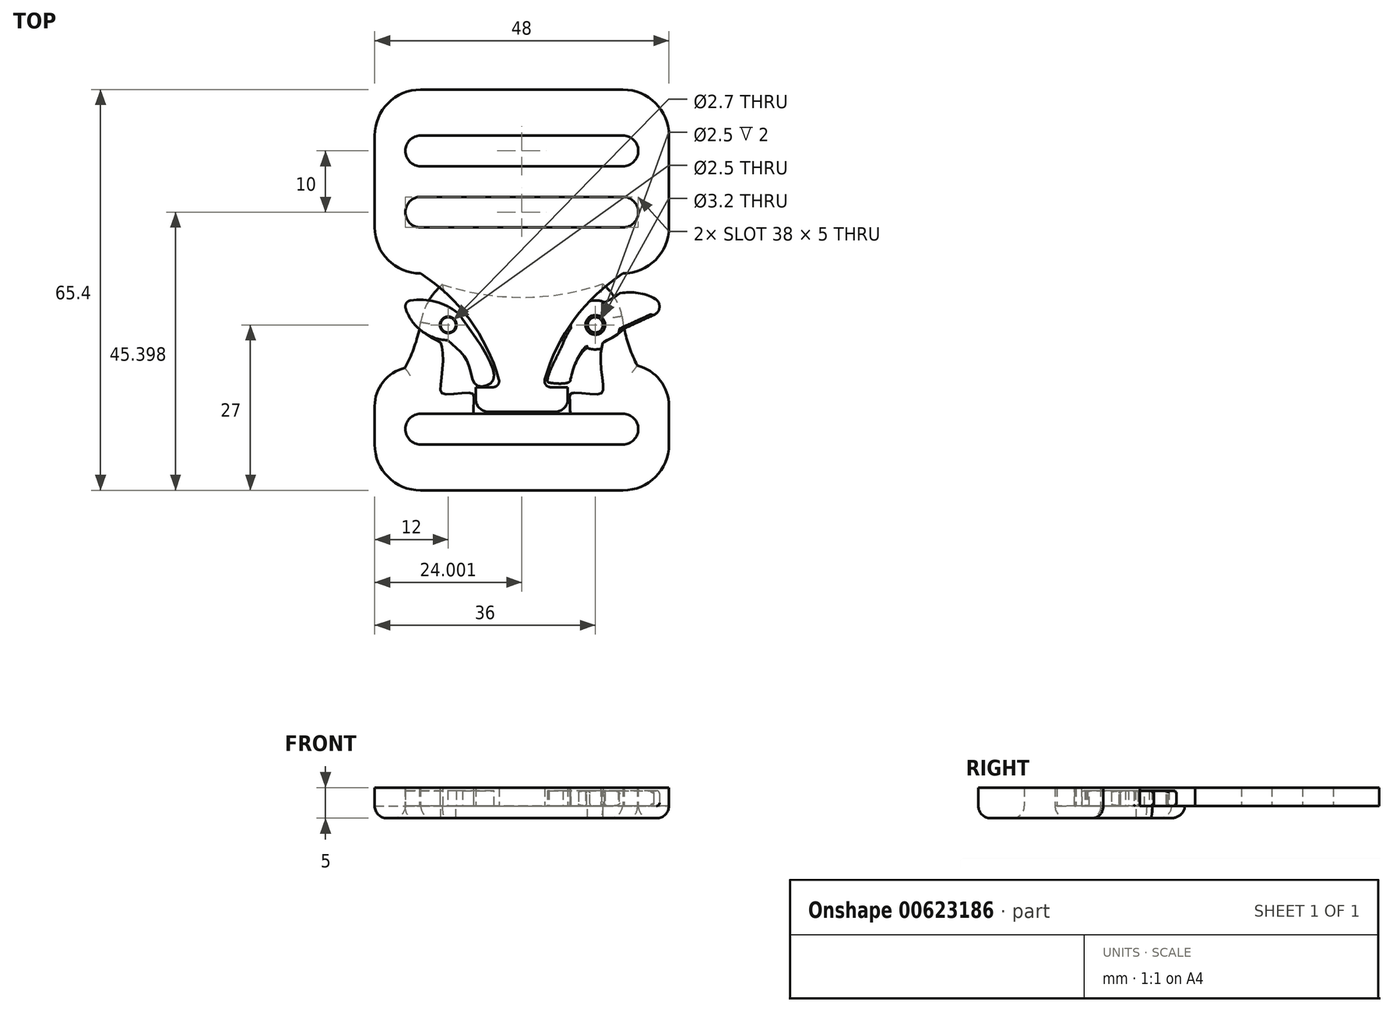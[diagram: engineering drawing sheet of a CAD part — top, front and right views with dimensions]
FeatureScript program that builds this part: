
annotation { "Feature Type Name" : "Feature", "Feature Type Description" : "" }
export const myFeature = defineFeature(function(context is Context, id is Id, definition is map)
    precondition{}
    {
        {
            var Q0;
            Q0=qCreatedBy(makeId("Top.planeOp"),FACE);
            var sketch = newSketch(context, id + "F0", { "sketchPlane" : qUnion([Q0])});
            skLineSegment(sketch, "E0.bottom", {"start": v(16.5, 2.5) * mm, "end": v(-16.5, 2.5) * mm});
            skLineSegment(sketch, "E0.top", {"start": v(16.5, -2.5) * mm, "end": v(-16.5, -2.5) * mm});
            skLineSegment(sketch, "E0.left", {"start": v(19, 0) * mm, "end": v(19, 0) * mm});
            skLineSegment(sketch, "E0.right", {"start": v(-19, 0) * mm, "end": v(-19, 0) * mm});
            skPoint(sketch, "E0.middle", {"position": v(0, 0) * mm});
            skPoint(sketch, "E1.visualSharp", {"position": v(-19, 2.5) * mm});
            skArc(sketch, "E1.filletArc", {"start": v(-16.5, 2.5) * mm, "mid": v(-18.27, 1.77) * mm, "end": v(-19, 0) * mm});
            skPoint(sketch, "E2.visualSharp", {"position": v(-19, -2.5) * mm});
            skArc(sketch, "E2.filletArc", {"start": v(-19, 0) * mm, "mid": v(-18.27, -1.77) * mm, "end": v(-16.5, -2.5) * mm});
            skPoint(sketch, "E3.visualSharp", {"position": v(19, -2.5) * mm});
            skArc(sketch, "E3.filletArc", {"start": v(16.5, -2.5) * mm, "mid": v(18.27, -1.77) * mm, "end": v(19, 0) * mm});
            skPoint(sketch, "E4.visualSharp", {"position": v(19, 2.5) * mm});
            skArc(sketch, "E4.filletArc", {"start": v(19, 0) * mm, "mid": v(18.27, 1.77) * mm, "end": v(16.5, 2.5) * mm});
            skLineSegment(sketch, "E5.bottom", {"start": v(16.5, -10) * mm, "end": v(-16.5, -10) * mm});
            skLineSegment(sketch, "E5.left", {"start": v(24, -2.5) * mm, "end": v(24, 3.75) * mm});
            skLineSegment(sketch, "E5.right", {"start": v(-24, -2.5) * mm, "end": v(-24, 3.75) * mm});
            skPoint(sketch, "E6.visualSharp", {"position": v(-24, -10) * mm});
            skArc(sketch, "E6.filletArc", {"start": v(-24, -2.5) * mm, "mid": v(-21.8, -7.8) * mm, "end": v(-16.5, -10) * mm});
            skPoint(sketch, "E7.visualSharp", {"position": v(24, -10) * mm});
            skArc(sketch, "E7.filletArc", {"start": v(16.5, -10) * mm, "mid": v(21.8, -7.8) * mm, "end": v(24, -2.5) * mm});
            skArc(sketch, "E8", {"start": v(-12.96, 23.6) * mm, "mid": v(0.12, 21.5) * mm, "end": v(13.2, 23.68) * mm});
            skLineSegment(sketch, "E9", {"start": v(0, 21.5) * mm, "end": v(0, 0) * mm, "construction": true});
            skArc(sketch, "E10", {"start": v(16.36, 18.4) * mm, "mid": v(17.24, 14.28) * mm, "end": v(18.84, 10.38) * mm});
            skArc(sketch, "E11", {"start": v(-19.07, 9.97) * mm, "mid": v(-17.47, 13.6) * mm, "end": v(-16.5, 17.47) * mm});
            skArc(sketch, "E12", {"start": v(16.5, 17.47) * mm, "mid": v(15.46, 20.9) * mm, "end": v(13.2, 23.68) * mm});
            skArc(sketch, "E13", {"start": v(-12.96, 23.6) * mm, "mid": v(-15.25, 20.83) * mm, "end": v(-16.5, 17.47) * mm});
            skArc(sketch, "E14", {"start": v(24, 3.75) * mm, "mid": v(22.56, 7.95) * mm, "end": v(18.84, 10.38) * mm});
            skArc(sketch, "E15", {"start": v(-19.07, 9.97) * mm, "mid": v(-22.62, 7.72) * mm, "end": v(-24, 3.75) * mm});
            skSolve(sketch);
        }
        {
            var Q0;
            Q0=qSketchRegion(id+"F0",true);
            extrude(context, id + "F1", {"entities" : qUnion([Q0]), "depth" : 2 * mm, "offsetDistance" : 25 * mm});
        }
        {
            var Q0;
            Q0=makeQuery(id+"F1.opExtrude","CAP_FACE",FACE,{"disambiguationData":[OSD([sQuery(id+"F0.wireOp",EDGE,"E0.bottom"),sQuery(id+"F0.wireOp",EDGE,"E0.top"),sQuery(id+"F0.wireOp",EDGE,"E1.filletArc"),sQuery(id+"F0.wireOp",EDGE,"E2.filletArc"),sQuery(id+"F0.wireOp",EDGE,"E3.filletArc"),sQuery(id+"F0.wireOp",EDGE,"E4.filletArc"),sQuery(id+"F0.wireOp",EDGE,"E5.bottom"),sQuery(id+"F0.wireOp",EDGE,"E5.left"),sQuery(id+"F0.wireOp",EDGE,"E5.right"),sQuery(id+"F0.wireOp",EDGE,"E6.filletArc"),sQuery(id+"F0.wireOp",EDGE,"E7.filletArc"),sQuery(id+"F0.wireOp",EDGE,"iaLIUP0t-tZGx-AWgD-4cdN-IuAON2PRfYnM.left"),sQuery(id+"F0.wireOp",EDGE,"iaLIUP0t-tZGx-AWgD-4cdN-IuAON2PRfYnM.right"),sQuery(id+"F0.wireOp",EDGE,"ac3eb495-d787-4141-9d20-389c025eaae5.filletArc"),sQuery(id+"F0.wireOp",EDGE,"95ab88b0-9d58-4345-83fa-b843aa859d97.filletArc"),sQuery(id+"F0.wireOp",EDGE,"E8")])],"isStart":false});
            var sketch = newSketch(context, id + "F2", { "sketchPlane" : qUnion([Q0])});
            skLineSegment(sketch, "E16.bottom", {"start": v(-16.5, 42.9) * mm, "end": v(16.5, 42.9) * mm});
            skLineSegment(sketch, "E16.top", {"start": v(-16.5, 47.9) * mm, "end": v(16.5, 47.9) * mm});
            skLineSegment(sketch, "E16.left", {"start": v(19, -8.96) * mm, "end": v(19, -8.96) * mm});
            skLineSegment(sketch, "E16.right", {"start": v(-19, -8.96) * mm, "end": v(-19, -8.96) * mm});
            skPoint(sketch, "E16.middle", {"position": v(0, 45.4) * mm});
            skPoint(sketch, "E17.visualSharp", {"position": v(19, 42.9) * mm});
            skArc(sketch, "E17.filletArc", {"start": v(16.5, 42.9) * mm, "mid": v(18.27, 43.63) * mm, "end": v(19, 45.4) * mm});
            skPoint(sketch, "E18.visualSharp", {"position": v(19, 47.9) * mm});
            skArc(sketch, "E18.filletArc", {"start": v(19, 45.4) * mm, "mid": v(18.27, 47.17) * mm, "end": v(16.5, 47.9) * mm});
            skPoint(sketch, "E19.visualSharp", {"position": v(-19, 47.9) * mm});
            skArc(sketch, "E19.filletArc", {"start": v(-16.5, 47.9) * mm, "mid": v(-18.27, 47.17) * mm, "end": v(-19, 45.4) * mm});
            skPoint(sketch, "E20.visualSharp", {"position": v(-19, 42.9) * mm});
            skArc(sketch, "E20.filletArc", {"start": v(-19, 45.4) * mm, "mid": v(-18.27, 43.63) * mm, "end": v(-16.5, 42.9) * mm});
            skLineSegment(sketch, "E21.bottom", {"start": v(-16.5, 55.4) * mm, "end": v(16.5, 55.4) * mm});
            skLineSegment(sketch, "E21.left", {"start": v(-24, 47.9) * mm, "end": v(-24, 35.4) * mm});
            skLineSegment(sketch, "E21.right", {"start": v(24, 47.9) * mm, "end": v(24, 35.4) * mm});
            skPoint(sketch, "E22.visualSharp", {"position": v(24, 55.4) * mm});
            skArc(sketch, "E22.filletArc", {"start": v(24, 47.9) * mm, "mid": v(21.8, 53.2) * mm, "end": v(16.5, 55.4) * mm});
            skPoint(sketch, "E23.visualSharp", {"position": v(-24, 55.4) * mm});
            skArc(sketch, "E23.filletArc", {"start": v(-16.5, 55.4) * mm, "mid": v(-21.8, 53.2) * mm, "end": v(-24, 47.9) * mm});
            skLineSegment(sketch, "E24.left", {"start": v(24, 35.4) * mm, "end": v(24, 32.9) * mm});
            skLineSegment(sketch, "E24.right", {"start": v(-24, 35.4) * mm, "end": v(-24, 32.9) * mm});
            skPoint(sketch, "E25.visualSharp", {"position": v(24, 20.4) * mm});
            skArc(sketch, "E25.filletArc", {"start": v(16.5, 25.4) * mm, "mid": v(21.8, 27.6) * mm, "end": v(24, 32.9) * mm});
            skPoint(sketch, "E26.visualSharp", {"position": v(-24, 20.4) * mm});
            skArc(sketch, "E26.filletArc", {"start": v(-24, 32.9) * mm, "mid": v(-21.8, 27.6) * mm, "end": v(-16.5, 25.4) * mm});
            skLineSegment(sketch, "E27", {"start": v(0, 45.4) * mm, "end": v(0, 35.4) * mm, "construction": true});
            skPoint(sketch, "E27.endSnap0", {"position": v(0, 42.9) * mm});
            skLineSegment(sketch, "E28.bottom", {"start": v(-16.5, 37.9) * mm, "end": v(16.5, 37.9) * mm});
            skLineSegment(sketch, "E28.top", {"start": v(-16.5, 32.9) * mm, "end": v(16.5, 32.9) * mm});
            skLineSegment(sketch, "E28.left", {"start": v(19, 1.04) * mm, "end": v(19, 1.04) * mm});
            skLineSegment(sketch, "E28.right", {"start": v(-19, 1.04) * mm, "end": v(-19, 1.04) * mm});
            skPoint(sketch, "E28.middle", {"position": v(0, 35.4) * mm});
            skPoint(sketch, "E29.visualSharp", {"position": v(19, 32.9) * mm});
            skArc(sketch, "E29.filletArc", {"start": v(16.5, 32.9) * mm, "mid": v(18.27, 33.63) * mm, "end": v(19, 35.4) * mm});
            skPoint(sketch, "E30.visualSharp", {"position": v(19, 37.9) * mm});
            skArc(sketch, "E30.filletArc", {"start": v(19, 35.4) * mm, "mid": v(18.27, 37.17) * mm, "end": v(16.5, 37.9) * mm});
            skPoint(sketch, "E31.visualSharp", {"position": v(-19, 37.9) * mm});
            skArc(sketch, "E31.filletArc", {"start": v(-16.5, 37.9) * mm, "mid": v(-18.27, 37.17) * mm, "end": v(-19, 35.4) * mm});
            skPoint(sketch, "E32.visualSharp", {"position": v(-19, 32.9) * mm});
            skArc(sketch, "E32.filletArc", {"start": v(-19, 35.4) * mm, "mid": v(-18.27, 33.63) * mm, "end": v(-16.5, 32.9) * mm});
            skArc(sketch, "E33", {"start": v(-16.5, 25.4) * mm, "mid": v(0, 21.84) * mm, "end": v(16.5, 25.4) * mm, "construction": true});
            skLineSegment(sketch, "E34", {"start": v(16.5, 25.4) * mm, "end": v(-16.5, 25.4) * mm, "construction": true});
            skLineSegment(sketch, "E35", {"start": v(0, 21.84) * mm, "end": v(0, 4.84) * mm, "construction": true});
            skPoint(sketch, "E35.endSnap0", {"position": v(0, 21.84) * mm});
            skLineSegment(sketch, "E36.bottom", {"start": v(7.5, 6.84) * mm, "end": v(4.7, 6.84) * mm});
            skLineSegment(sketch, "E36.top", {"start": v(5.5, 2.84) * mm, "end": v(-5.5, 2.84) * mm});
            skLineSegment(sketch, "E36.left", {"start": v(7.5, 6.84) * mm, "end": v(7.5, 4.84) * mm});
            skLineSegment(sketch, "E36.right", {"start": v(-7.5, 6.84) * mm, "end": v(-7.5, 4.84) * mm});
            skPoint(sketch, "E36.middle", {"position": v(0, 4.84) * mm});
            skLineSegment(sketch, "E37", {"start": v(16.5, 25.4) * mm, "end": v(16.5, 55.4) * mm, "construction": true});
            skLineSegment(sketch, "E38", {"start": v(-16.5, 25.4) * mm, "end": v(-16.5, 55.4) * mm, "construction": true});
            skPoint(sketch, "E39.visualSharp", {"position": v(7.5, 2.84) * mm});
            skArc(sketch, "E39.filletArc", {"start": v(5.5, 2.84) * mm, "mid": v(6.91, 3.42) * mm, "end": v(7.5, 4.84) * mm});
            skPoint(sketch, "E40.visualSharp", {"position": v(-7.5, 2.84) * mm});
            skArc(sketch, "E40.filletArc", {"start": v(-7.5, 4.84) * mm, "mid": v(-6.91, 3.42) * mm, "end": v(-5.5, 2.84) * mm});
            skLineSegment(sketch, "E41", {"start": v(0, 4.84) * mm, "end": v(3, 4.84) * mm, "construction": true});
            skLineSegment(sketch, "E42", {"start": v(0, 4.84) * mm, "end": v(-3, 4.84) * mm, "construction": true});
            skArc(sketch, "E43", {"start": v(16.5, 25.4) * mm, "mid": v(8.57, 17.9) * mm, "end": v(3.75, 8.11) * mm});
            skArc(sketch, "E44", {"start": v(-3.73, 8.1) * mm, "mid": v(-8.54, 17.91) * mm, "end": v(-16.5, 25.4) * mm});
            skLineSegment(sketch, "E45.trimOffspring", {"start": v(-4.7, 6.84) * mm, "end": v(-7.5, 6.84) * mm});
            skPoint(sketch, "E46.visualSharp", {"position": v(3.41, 6.84) * mm});
            skArc(sketch, "E46.filletArc", {"start": v(3.75, 8.11) * mm, "mid": v(3.91, 7.23) * mm, "end": v(4.7, 6.84) * mm});
            skPoint(sketch, "E47.visualSharp", {"position": v(-3.4, 6.84) * mm});
            skArc(sketch, "E47.filletArc", {"start": v(-4.7, 6.84) * mm, "mid": v(-3.9, 7.23) * mm, "end": v(-3.73, 8.1) * mm});
            skSolve(sketch);
        }
        {
            var Q0;
            Q0=qSketchRegion(id+"F2",true);
            extrude(context, id + "F3", {"entities" : qUnion([Q0]), "depth" : 3 * mm, "offsetDistance" : 25 * mm});
        }
        {
            var Q0;
            Q0=makeQuery(id+"F1.opExtrude","CAP_FACE",FACE,{"disambiguationData":[OSD([sQuery(id+"F0.wireOp",EDGE,"E0.bottom"),sQuery(id+"F0.wireOp",EDGE,"E0.top"),sQuery(id+"F0.wireOp",EDGE,"E1.filletArc"),sQuery(id+"F0.wireOp",EDGE,"E2.filletArc"),sQuery(id+"F0.wireOp",EDGE,"E3.filletArc"),sQuery(id+"F0.wireOp",EDGE,"E4.filletArc"),sQuery(id+"F0.wireOp",EDGE,"E5.bottom"),sQuery(id+"F0.wireOp",EDGE,"E5.left"),sQuery(id+"F0.wireOp",EDGE,"E5.right"),sQuery(id+"F0.wireOp",EDGE,"E6.filletArc"),sQuery(id+"F0.wireOp",EDGE,"E7.filletArc"),sQuery(id+"F0.wireOp",EDGE,"E8"),sQuery(id+"F0.wireOp",EDGE,"E10"),sQuery(id+"F0.wireOp",EDGE,"E11"),sQuery(id+"F0.wireOp",EDGE,"E12"),sQuery(id+"F0.wireOp",EDGE,"E13"),sQuery(id+"F0.wireOp",EDGE,"E14"),sQuery(id+"F0.wireOp",EDGE,"E15")])],"isStart":false});
            var sketch = newSketch(context, id + "F4", { "sketchPlane" : qUnion([Q0])});
            skArc(sketch, "E48.0.2", {"start": v(-16.71, 16.34) * mm, "mid": v(-17.66, 13.07) * mm, "end": v(-19.07, 9.97) * mm});
            skArc(sketch, "E48.0.3", {"start": v(-19.07, 9.97) * mm, "mid": v(-22.62, 7.72) * mm, "end": v(-24, 3.75) * mm});
            skLineSegment(sketch, "E48.0.4", {"start": v(-24, 3.75) * mm, "end": v(-24, -2.5) * mm});
            skArc(sketch, "E48.0.5", {"start": v(-24, -2.5) * mm, "mid": v(-21.8, -7.8) * mm, "end": v(-16.5, -10) * mm});
            skLineSegment(sketch, "E48.0.6", {"start": v(-16.5, -10) * mm, "end": v(16.5, -10) * mm});
            skArc(sketch, "E48.0.7", {"start": v(16.5, -10) * mm, "mid": v(21.8, -7.8) * mm, "end": v(24, -2.5) * mm});
            skLineSegment(sketch, "E48.0.8", {"start": v(24, -2.5) * mm, "end": v(24, 3.75) * mm});
            skArc(sketch, "E48.0.9", {"start": v(24, 3.75) * mm, "mid": v(22.56, 7.95) * mm, "end": v(18.84, 10.38) * mm});
            skArc(sketch, "E48.0.10", {"start": v(18.84, 10.38) * mm, "mid": v(17.57, 13.28) * mm, "end": v(16.7, 16.33) * mm});
            skFitSpline(sketch, "E49", {"points": [v(16.79, 16.4) * mm, v(15.52, 15.41) * mm, v(13.35, 14.18) * mm, v(13.27, 14.13) * mm, v(12.86, 11.88) * mm, v(13.27, 6.62) * mm, v(12.68, 5.7) * mm, v(8.19, 5.85) * mm, v(7.83, 5.04) * mm, v(7.92, 2) * mm], "startDerivative": vector(-10.18, -9.13) * mm, "endDerivative": vector(0.88, -25.22) * mm});
            skLineSegment(sketch, "E50", {"start": v(0, 0) * mm, "end": v(0, 16.05) * mm, "construction": true});
            skFitSpline(sketch, "E51.MirrorCS", {"points": [v(-16.79, 16.4) * mm, v(-15.52, 15.41) * mm, v(-13.35, 14.18) * mm, v(-13.27, 14.13) * mm, v(-12.86, 11.88) * mm, v(-13.27, 6.62) * mm, v(-12.68, 5.7) * mm, v(-8.19, 5.85) * mm, v(-7.83, 5.04) * mm, v(-7.92, 2) * mm], "startDerivative": vector(10.18, -9.13) * mm, "endDerivative": vector(-0.88, -25.22) * mm});
            skPoint(sketch, "E48.0.11.end.orphan", {"position": v(13.2, 23.68) * mm});
            skPoint(sketch, "E52.orphan", {"position": v(16.36, 18.4) * mm});
            skPoint(sketch, "E48.0.1.start.orphan", {"position": v(-12.96, 23.6) * mm});
            skPoint(sketch, "E53.orphan", {"position": v(-16.5, 17.47) * mm});
            skSolve(sketch);
        }
        {
            var Q0;
            {var subQ4=sQuery(id+"F4.wireOp",EDGE,"E48.0.2");Q0=makeQuery(id+"F4.imprint","IMPRINT",FACE,{"disambiguationData":[TD([[makeQuery(id+"F4.imprint","IMPRINT",EDGE,{"derivedFrom":subQ4}),-1.0]])]});}
            extrude(context, id + "F5", {"entities" : qUnion([Q0]), "operationType" : NewBodyOperationType.ADD, "depth" : 3 * mm, "offsetDistance" : 25 * mm});
        }
        {
            var Q0;
            Q0=makeQuery(id+"F2.imprint","IMPRINT",FACE,{"disambiguationData":[TD([[makeQuery(id+"F2.imprint","IMPRINT",EDGE,{"derivedFrom":sQuery(id+"F2.wireOp",EDGE,"E36.bottom")}),-1.0]])]});
            var sketch = newSketch(context, id + "F6", { "sketchPlane" : qUnion([Q0])});
            skLineSegment(sketch, "E54", {"start": v(0, 0) * mm, "end": v(0, 17) * mm, "construction": true});
            skLineSegment(sketch, "E55", {"start": v(0, 17) * mm, "end": v(12, 17) * mm, "construction": true});
            skLineSegment(sketch, "E56", {"start": v(0, 17) * mm, "end": v(-12, 17) * mm, "construction": true});
            skLineSegment(sketch, "E57", {"start": v(11.27, 19.4) * mm, "end": v(11.27, 19.4) * mm});
            skArc(sketch, "E58", {"start": v(-12.1, 14.5) * mm, "mid": v(-9.66, 16.13) * mm, "end": v(-10.44, 18.96) * mm});
            skLineSegment(sketch, "E59", {"start": v(0, 20) * mm, "end": v(21, 20) * mm, "construction": true});
            skLineSegment(sketch, "E60", {"start": v(0, 20) * mm, "end": v(-18, 20) * mm, "construction": true});
            skArc(sketch, "E61", {"start": v(-18.16, 20.99) * mm, "mid": v(-18.85, 20.52) * mm, "end": v(-18.95, 19.7) * mm});
            skLineSegment(sketch, "E62", {"start": v(0, 17) * mm, "end": v(0, 20) * mm, "construction": true});
            skArc(sketch, "E63", {"start": v(21.5, 18.6) * mm, "mid": v(21.61, 18.67) * mm, "end": v(21.73, 18.73) * mm});
            skArc(sketch, "E64", {"start": v(-18.95, 19.7) * mm, "mid": v(-16.34, 16.02) * mm, "end": v(-12.1, 14.5) * mm});
            skArc(sketch, "E65", {"start": v(-10.44, 18.96) * mm, "mid": v(-14.09, 20.78) * mm, "end": v(-18.16, 20.99) * mm});
            skCircle(sketch, "E66", {"center": v(12, 17) * mm, "radius": 1.6 * mm});
            skCircle(sketch, "E67", {"center": v(-12, 17) * mm, "radius": 1.35 * mm});
            skFitSpline(sketch, "E68", {"points": [v(-10.44, 18.96) * mm, v(-4.72, 7.9) * mm, v(-7.43, 7.2) * mm, v(-8.69, 10.61) * mm, v(-12.1, 14.5) * mm], "startDerivative": vector(26.9, -36.54) * mm, "endDerivative": vector(-17.44, 14.5) * mm});
            skFitSpline(sketch, "E69", {"points": [v(6.74, 14) * mm, v(4.4, 7.58) * mm, v(7.49, 10.39) * mm], "startDerivative": vector(-1.72, -5.28) * mm, "endDerivative": vector(-7, -0.02) * mm});
            skFitSpline(sketch, "E70", {"points": [v(12.96, 14.7) * mm, v(21.5, 18.6) * mm], "startDerivative": vector(0.83, 0.4) * mm, "endDerivative": vector(0.83, 0.4) * mm});
            skFitSpline(sketch, "E71", {"points": [v(4.4, 7.58) * mm, v(6.08, 7.42) * mm, v(7.9, 7.86) * mm, v(7.43, 10.4) * mm], "startDerivative": vector(5.45, -0.72) * mm, "endDerivative": vector(0.06, 9.56) * mm});
            skArc(sketch, "E72", {"start": v(21.78, 21.25) * mm, "mid": v(18.94, 22.22) * mm, "end": v(15.94, 22.14) * mm});
            skArc(sketch, "E73", {"start": v(21.6, 18.66) * mm, "mid": v(22.46, 19.9) * mm, "end": v(21.78, 21.25) * mm});
            skPoint(sketch, "E74", {"position": v(15.94, 22.14) * mm});
            skArc(sketch, "E75", {"start": v(11.84, 20) * mm, "mid": v(13.98, 20.9) * mm, "end": v(15.94, 22.14) * mm});
            skPoint(sketch, "E76", {"position": v(4.6, 9.42) * mm});
            skArc(sketch, "E77", {"start": v(4.6, 9.42) * mm, "mid": v(4.57, 9) * mm, "end": v(4.65, 8.58) * mm});
            skPoint(sketch, "E78", {"position": v(4.65, 8.58) * mm});
            skPoint(sketch, "E79", {"position": v(6.98, 7.46) * mm});
            skArc(sketch, "E80", {"start": v(4.65, 8.58) * mm, "mid": v(5.7, 7.8) * mm, "end": v(6.98, 7.46) * mm});
            skArc(sketch, "E81", {"start": v(11.84, 20) * mm, "mid": v(8.76, 17.45) * mm, "end": v(6.74, 14) * mm});
            skArc(sketch, "E82", {"start": v(9.25, 11.72) * mm, "mid": v(8.42, 9.84) * mm, "end": v(7.9, 7.86) * mm});
            skArc(sketch, "E83", {"start": v(12.96, 14.7) * mm, "mid": v(10.87, 13.5) * mm, "end": v(9.25, 11.72) * mm});
            skSolve(sketch);
        }
        {
            var Q0;
            Q0=qSketchRegion(id+"F6",true);
            extrude(context, id + "F7", {"entities" : qUnion([Q0]), "depth" : 2.5 * mm, "offsetDistance" : 25 * mm});
        }
        {
            var Q0;
            Q0=makeQuery(id+"F1.opExtrude","CAP_FACE",FACE,{"disambiguationData":[OSD([sQuery(id+"F0.wireOp",EDGE,"E0.bottom"),sQuery(id+"F0.wireOp",EDGE,"E0.top"),sQuery(id+"F0.wireOp",EDGE,"E1.filletArc"),sQuery(id+"F0.wireOp",EDGE,"E2.filletArc"),sQuery(id+"F0.wireOp",EDGE,"E3.filletArc"),sQuery(id+"F0.wireOp",EDGE,"E4.filletArc"),sQuery(id+"F0.wireOp",EDGE,"E5.bottom"),sQuery(id+"F0.wireOp",EDGE,"E5.left"),sQuery(id+"F0.wireOp",EDGE,"E5.right"),sQuery(id+"F0.wireOp",EDGE,"E6.filletArc"),sQuery(id+"F0.wireOp",EDGE,"E7.filletArc"),sQuery(id+"F0.wireOp",EDGE,"E8"),sQuery(id+"F0.wireOp",EDGE,"E10"),sQuery(id+"F0.wireOp",EDGE,"E11"),sQuery(id+"F0.wireOp",EDGE,"E12"),sQuery(id+"F0.wireOp",EDGE,"E13"),sQuery(id+"F0.wireOp",EDGE,"E14"),sQuery(id+"F0.wireOp",EDGE,"E15")])],"isStart":true});
            fillet(context, id + "F8", {"entities" : qUnion([Q0]), "radius" : 2 * mm, "tangentPropagation" : true, "allowEdgeOverflow" : false});
        }
        {
            var Q0;
            Q0=makeQuery(id+"F1.opExtrude","CAP_FACE",FACE,{"disambiguationData":[OSD([sQuery(id+"F0.wireOp",EDGE,"E0.bottom"),sQuery(id+"F0.wireOp",EDGE,"E0.top"),sQuery(id+"F0.wireOp",EDGE,"E1.filletArc"),sQuery(id+"F0.wireOp",EDGE,"E2.filletArc"),sQuery(id+"F0.wireOp",EDGE,"E3.filletArc"),sQuery(id+"F0.wireOp",EDGE,"E4.filletArc"),sQuery(id+"F0.wireOp",EDGE,"E5.bottom"),sQuery(id+"F0.wireOp",EDGE,"E5.left"),sQuery(id+"F0.wireOp",EDGE,"E5.right"),sQuery(id+"F0.wireOp",EDGE,"E6.filletArc"),sQuery(id+"F0.wireOp",EDGE,"E7.filletArc"),sQuery(id+"F0.wireOp",EDGE,"E8"),sQuery(id+"F0.wireOp",EDGE,"E10"),sQuery(id+"F0.wireOp",EDGE,"E11"),sQuery(id+"F0.wireOp",EDGE,"E12"),sQuery(id+"F0.wireOp",EDGE,"E13"),sQuery(id+"F0.wireOp",EDGE,"E14"),sQuery(id+"F0.wireOp",EDGE,"E15")])],"isStart":false});
            var sketch = newSketch(context, id + "F9", { "sketchPlane" : qUnion([Q0])});
            skLineSegment(sketch, "E84", {"start": v(0, 0) * mm, "end": v(0, 17) * mm, "construction": true});
            skLineSegment(sketch, "E85", {"start": v(0, 17) * mm, "end": v(12, 17) * mm, "construction": true});
            skLineSegment(sketch, "E86", {"start": v(0, 17) * mm, "end": v(-12, 17) * mm, "construction": true});
            skCircle(sketch, "E87", {"center": v(-12, 17) * mm, "radius": 1.25 * mm});
            skCircle(sketch, "E88", {"center": v(12, 17) * mm, "radius": 1.25 * mm});
            skSolve(sketch);
        }
        {
            var Q0;
            Q0=qSketchRegion(id+"F9",true);
            extrude(context, id + "F10", {"entities" : qUnion([Q0]), "operationType" : NewBodyOperationType.REMOVE, "oppositeDirection" : true, "depth" : 2 * mm, "offsetDistance" : 25 * mm});
        }
        {
            var Q0;
            Q0=makeQuery(id+"F7.opExtrude","CAP_EDGE",EDGE,{"disambiguationData":[OSD([sQuery(id+"F6.wireOp",EDGE,"E66")])],"isStart":false});
            var Q1;
            Q1=makeQuery(id+"F7.opExtrude","CAP_EDGE",EDGE,{"disambiguationData":[OSD([sQuery(id+"F6.wireOp",EDGE,"E66")])],"isStart":true});
            fillet(context, id + "F11", {"entities" : qUnion([Q0, Q1]), "radius" : .5 * mm, "tangentPropagation" : true, "allowEdgeOverflow" : false});
        }
        {
            var Q0;
            Q0=makeQuery(id+"F7.opExtrude","SWEPT_FACE",FACE,{"disambiguationData":[OSD([sQuery(id+"F6.wireOp",EDGE,"E73")])]});
            var Q1;
            Q1=makeQuery(id+"F7.opExtrude","SWEPT_FACE",FACE,{"disambiguationData":[OSD([sQuery(id+"F6.wireOp",EDGE,"E72")])]});
            fillet(context, id + "F12", {"entities" : qUnion([Q0, Q1]), "radius" : .5 * mm, "allowEdgeOverflow" : false});
        }
        {
            var Q0;
            Q0=makeQuery(id+"F7.opExtrude","CAP_EDGE",EDGE,{"disambiguationData":[OSD([sQuery(id+"F6.wireOp",EDGE,"E70")])],"isStart":false});
            var Q1;
            Q1=makeQuery(id+"F7.opExtrude","CAP_EDGE",EDGE,{"disambiguationData":[OSD([sQuery(id+"F6.wireOp",EDGE,"E70")])],"isStart":true});
            fillet(context, id + "F13", {"entities" : qUnion([Q0, Q1]), "radius" : .3 * mm, "tangentPropagation" : true, "allowEdgeOverflow" : false});
        }
        {
            var Q0;
            Q0=makeQuery(id+"F7.opExtrude","CAP_FACE",FACE,{"disambiguationData":[OSD([sQuery(id+"F6.wireOp",EDGE,"E63"),sQuery(id+"F6.wireOp",EDGE,"E66"),sQuery(id+"F6.wireOp",EDGE,"E69"),sQuery(id+"F6.wireOp",EDGE,"E70"),sQuery(id+"F6.wireOp",EDGE,"E71"),sQuery(id+"F6.wireOp",EDGE,"E72"),sQuery(id+"F6.wireOp",EDGE,"E73"),sQuery(id+"F6.wireOp",EDGE,"E75"),sQuery(id+"F6.wireOp",EDGE,"E77"),sQuery(id+"F6.wireOp",EDGE,"E80"),sQuery(id+"F6.wireOp",EDGE,"E81"),sQuery(id+"F6.wireOp",EDGE,"E82"),sQuery(id+"F6.wireOp",EDGE,"E83")])],"isStart":false});
            var sketch = newSketch(context, id + "F14", { "sketchPlane" : qUnion([Q0])});
            skCircle(sketch, "E89", {"center": v(12, 17) * mm, "radius": 1.6 * mm});
            skCircle(sketch, "E90", {"center": v(12, 17) * mm, "radius": 4 * mm});
            skSolve(sketch);
        }
        {
            var Q0;
            Q0 = qSketchRegion(id + "F14", true);
            extrude(context, id + "F15", {"entities" : qUnion([Q0]), "operationType" : NewBodyOperationType.ADD, "oppositeDirection" : true, "depth" : 2.5 * mm, "offsetDistance" : 25 * mm});
        }
        {
            var Q0;
            {var subQ0=sQuery(id+"F14.wireOp",EDGE,"E90");var subQ2=sQuery(id+"F6.wireOp",EDGE,"E82");Q0=makeQuery(id+"F15.boolean.opBoolean","SPLIT",EDGE,{"disambiguationData":[TD([makeQuery(id+"F7.opExtrude","SWEPT_FACE",FACE,{"disambiguationData":[OSD([subQ2])]})])],"derivedFrom":makeQuery(id+"F15.opExtrude","CAP_EDGE",EDGE,{"disambiguationData":[OSD([subQ0])],"isStart":true})});}
            var Q1;
            {var subQ1=sQuery(id+"F14.wireOp",EDGE,"E90");var subQ2=sQuery(id+"F6.wireOp",EDGE,"E75");Q1=makeQuery(id+"F15.boolean.opBoolean","SPLIT",EDGE,{"disambiguationData":[TD([makeQuery(id+"F7.opExtrude","SWEPT_FACE",FACE,{"disambiguationData":[OSD([subQ2])]})])],"derivedFrom":makeQuery(id+"F15.opExtrude","CAP_EDGE",EDGE,{"disambiguationData":[OSD([subQ1])],"isStart":true})});}
            var Q2;
            {var subQ0=sQuery(id+"F14.wireOp",EDGE,"E90");var subQ2=sQuery(id+"F6.wireOp",EDGE,"E82");Q2=makeQuery(id+"F15.boolean.opBoolean","SPLIT",EDGE,{"disambiguationData":[TD([makeQuery(id+"F7.opExtrude","SWEPT_FACE",FACE,{"disambiguationData":[OSD([subQ2])]})])],"derivedFrom":makeQuery(id+"F15.opExtrude","CAP_EDGE",EDGE,{"disambiguationData":[OSD([subQ0])],"isStart":false})});}
            var Q3;
            {var subQ0=sQuery(id+"F14.wireOp",EDGE,"E90");var subQ1=sQuery(id+"F6.wireOp",EDGE,"E75");Q3=makeQuery(id+"F15.boolean.opBoolean","SPLIT",EDGE,{"disambiguationData":[TD([makeQuery(id+"F7.opExtrude","SWEPT_FACE",FACE,{"disambiguationData":[OSD([subQ1])]})])],"derivedFrom":makeQuery(id+"F15.opExtrude","CAP_EDGE",EDGE,{"disambiguationData":[OSD([subQ0])],"isStart":false})});}
            fillet(context, id + "F16", {"entities" : qUnion([Q0, Q1, Q2, Q3]), "radius" : 0.4 * mm, "tangentPropagation" : true, "allowEdgeOverflow" : false});
        }
        {
            var Q0;
            Q0=makeQuery(id+"F15.boolean.opBoolean","MERGE",FACE,{"derivedFrom":[makeQuery(id+"F7.opExtrude","SWEPT_FACE",FACE,{"disambiguationData":[OSD([sQuery(id+"F6.wireOp",EDGE,"E66")])]}),makeQuery(id+"F15.opExtrude","SWEPT_FACE",FACE,{"disambiguationData":[OSD([sQuery(id+"F14.wireOp",EDGE,"E89")])]})]});
            fillet(context, id + "F17", {"entities" : qUnion([Q0]), "radius" : .2 * mm, "tangentPropagation" : true, "allowEdgeOverflow" : false});
        }
    });
